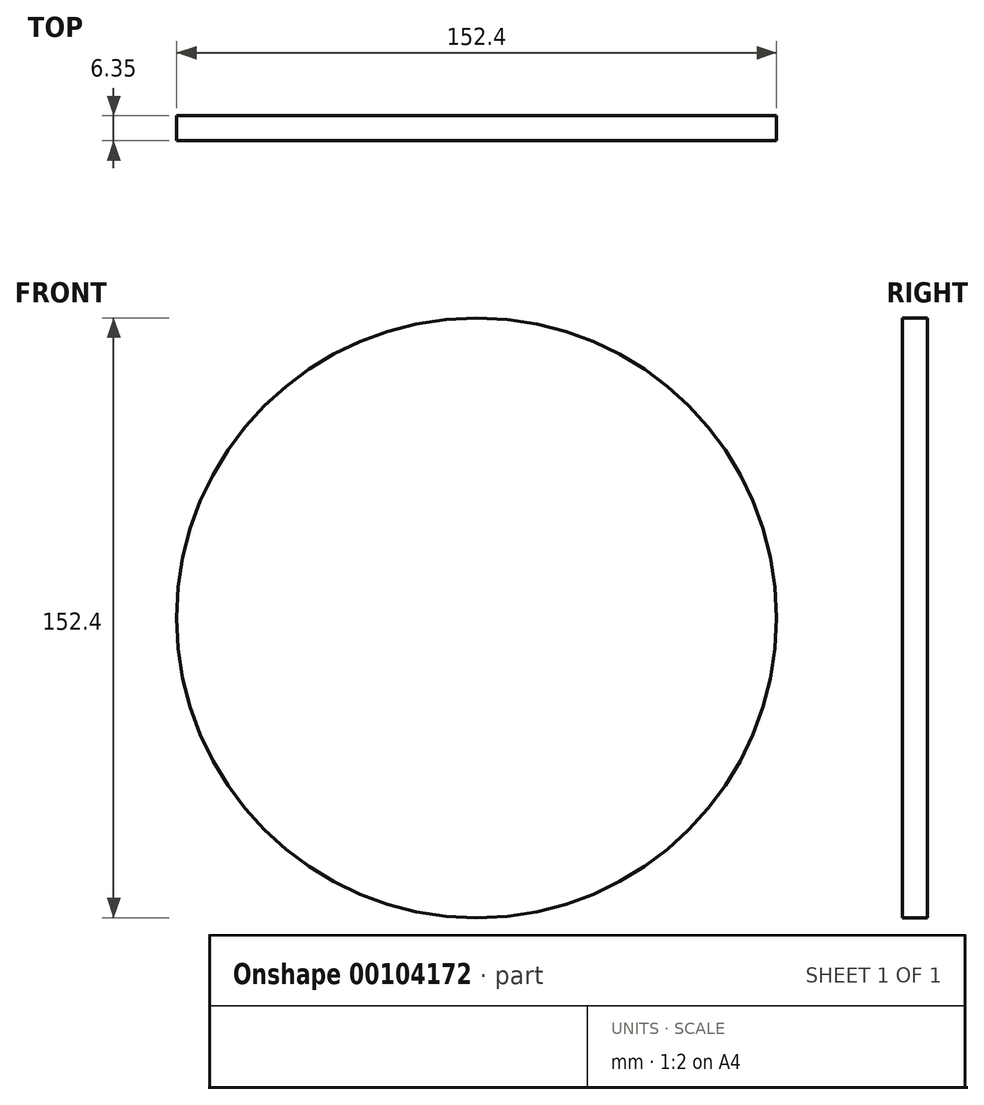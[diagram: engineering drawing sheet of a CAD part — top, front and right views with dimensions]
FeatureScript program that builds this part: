
annotation { "Feature Type Name" : "Feature", "Feature Type Description" : "" }
export const myFeature = defineFeature(function(context is Context, id is Id, definition is map)
    precondition{}
    {
        {
            var Q0;
            Q0=qCreatedBy(makeId("Front.planeOp"),FACE);
            var sketch = newSketch(context, id + "F0", { "sketchPlane" : qUnion([Q0])});
            skCircle(sketch, "E0", {"center": v(-13.21, 23.33) * mm, "radius": 76.2 * mm});
            skSolve(sketch);
        }
        {
            var Q0;
            Q0=makeQuery(id+"F0.imprint","IMPRINT",FACE,{"disambiguationData":[TD([[makeQuery(id+"F0.imprint","IMPRINT",EDGE,{"derivedFrom":sQuery(id+"F0.wireOp",EDGE,"E0")}),1.0]])]});
            extrude(context, id + "F1", {"entities" : qUnion([Q0]), "depth" : 6.35 * mm});
        }
    });
